# Revit family: DSI-600-Elevator-Smoke-Containment-Systems
name_source: partatom
category: Doors
units: mm (PartAtom-declared; Revit-internal decimal feet)

## family parameters
Always vertical = Yes
Cut with Voids When Loaded = No
Host = Wall
OmniClass Number = 23.30.60.17
OmniClass Title = Fire and Smoke Shutters and Curtains
Room Calculation Point = No
Shared = No

## types (3) — shared parameters
Analytic Construction = <None>
CAD Details = https://www.arcat.com
CurtainDrop_Viz = Yes
Define Thermal Properties by = Schematic Type
Description = Elevator Smoke Containment System
Fire Performance = UL 10D 1 HR  ;  California Fire State Marshall
Frame Width = 0' - 4"
FrameDepth = 0' - 2"
Keynote = 08 34 85
Manufacturer = Door Systems
Model = DSI-600
Product Page URL = https://www.arcat.com
Rough Height = 0' - 0"
Rough Width = 0' - 0"
Specification = http://www.arcat.com
Standards Conformance = ICC  ;  UL 1784 S Label  ;  UL 864  ;  OSHPD  ;  LAFD High Rise
URL = https://www.doorsysinc.com
Wall Closure = By host

## type names
- Multiple Roller Side by Side
- Multiple Roller Over Under
- Single Roller
type visibility flags (boolean, named after types; folded from table):
- Multiple Roller Side by Side: Yes: Multiple Roller Side by Side
- Multiple Roller Over Under: Yes: Multiple Roller Over Under
- Single Roller: Yes: (none)

## geometry (parser evidence)
native form markers: Sweep x2
no freeform markers — native parametric forms only
